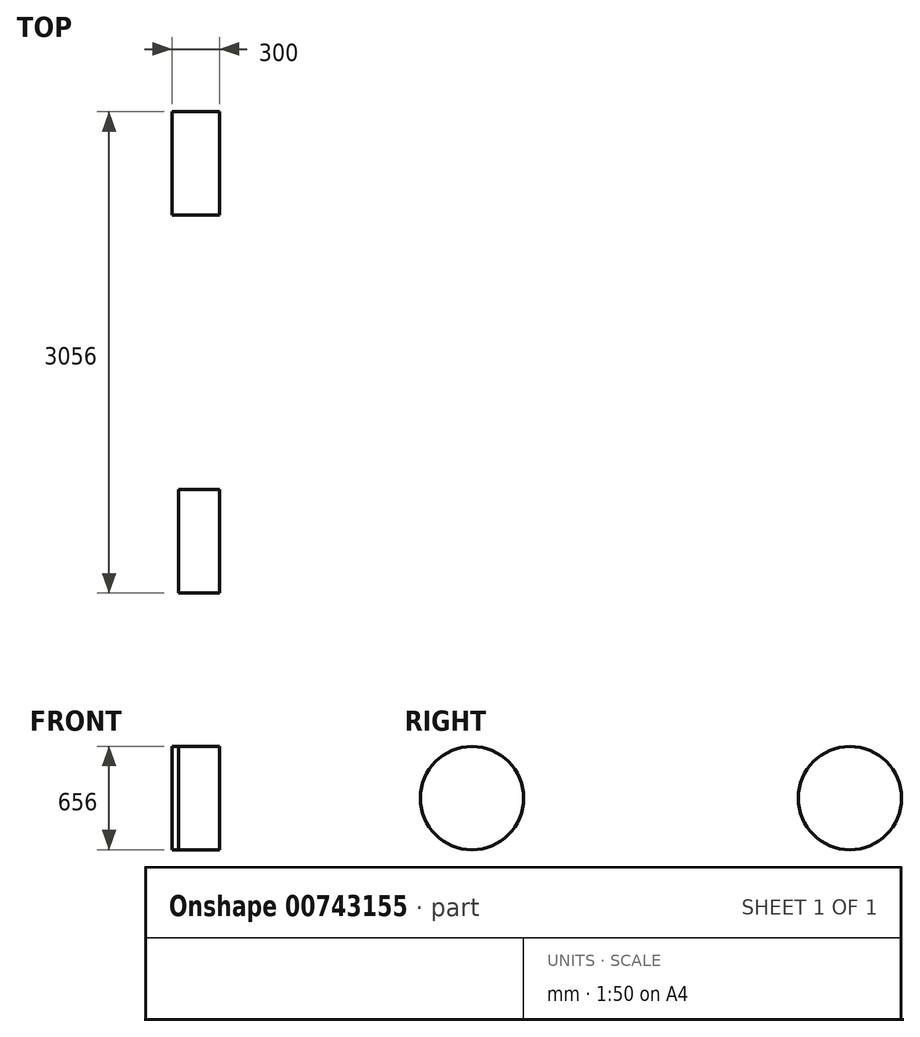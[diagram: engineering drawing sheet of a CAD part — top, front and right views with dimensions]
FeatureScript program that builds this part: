
annotation { "Feature Type Name" : "Feature", "Feature Type Description" : "" }
export const myFeature = defineFeature(function(context is Context, id is Id, definition is map)
    precondition{}
    {
        {
            var Q0;
            Q0=qCreatedBy(makeId("Right.planeOp"),FACE);
            var sketch = newSketch(context, id + "F0", { "sketchPlane" : qUnion([Q0])});
            skCircle(sketch, "E0", {"center": v(-865.86, -88.17) * mm, "radius": 328 * mm});
            skCircle(sketch, "E1", {"center": v(1534.14, -88.17) * mm, "radius": 328 * mm});
            skArc(sketch, "E2", {"start": v(-515.86, -88.17) * mm, "mid": v(-865.86, 261.83) * mm, "end": v(-1215.86, -88.17) * mm});
            skArc(sketch, "E3", {"start": v(1884.14, -88.17) * mm, "mid": v(1534.14, 261.83) * mm, "end": v(1184.14, -88.17) * mm});
            skCircle(sketch, "E4", {"center": v(-865.86, -88.17) * mm, "radius": 254 * mm});
            skCircle(sketch, "E5", {"center": v(1534.14, -88.17) * mm, "radius": 254 * mm});
            skLineSegment(sketch, "E6", {"start": v(-515.86, -88.17) * mm, "end": v(-515.86, -342.17) * mm});
            skLineSegment(sketch, "E7", {"start": v(-515.86, -342.17) * mm, "end": v(1184.14, -342.17) * mm});
            skLineSegment(sketch, "E8", {"start": v(1184.14, -342.17) * mm, "end": v(1184.14, -88.17) * mm});
            skLineSegment(sketch, "E9", {"start": v(-865.86, -342.17) * mm, "end": v(1534.14, -342.17) * mm, "construction": true});
            skLineSegment(sketch, "E10", {"start": v(-1215.86, -88.17) * mm, "end": v(-1215.86, -342.17) * mm});
            skLineSegment(sketch, "E11", {"start": v(-1215.86, -342.17) * mm, "end": v(-1715.86, -342.17) * mm});
            skLineSegment(sketch, "E12", {"start": v(-865.86, -342.17) * mm, "end": v(-2003.44, -342.17) * mm, "construction": true});
            skLineSegment(sketch, "E13", {"start": v(-1715.86, -342.17) * mm, "end": v(-1615.86, -282.17) * mm});
            skLineSegment(sketch, "E14", {"start": v(-1615.86, -282.17) * mm, "end": v(-1715.86, -62.17) * mm});
            skFitSpline(sketch, "E15", {"points": [v(-1715.86, -62.17) * mm, v(-865.86, 311.83) * mm, v(-65.86, 237.83) * mm, v(694.14, 237.83) * mm, v(1534.14, 311.83) * mm, v(1999.14, 201.83) * mm], "startDerivative": vector(5740.96, 4050.88) * mm, "endDerivative": vector(2088.55, 269.29) * mm});
            skFitSpline(sketch, "E16", {"points": [v(1999.14, 201.83) * mm, v(1884.14, -88.17) * mm], "startDerivative": vector(-161.5, -271.03) * mm, "endDerivative": vector(-344.1, -698.66) * mm});
            skLineSegment(sketch, "E17", {"start": v(-605.86, 300.17) * mm, "end": v(-105.86, 631.83) * mm});
            skFitSpline(sketch, "E18", {"points": [v(-105.86, 631.83) * mm, v(705.51, 627.45) * mm, v(1401.65, 430.3) * mm], "startDerivative": vector(1350.4, 204.52) * mm, "endDerivative": vector(1584.08, -729.05) * mm});
            skFitSpline(sketch, "E19", {"points": [v(1401.65, 430.3) * mm, v(1819.73, 233.23) * mm], "startDerivative": vector(436.87, -218.43) * mm, "endDerivative": vector(749.4, -276.18) * mm});
            skLineSegment(sketch, "E20", {"start": v(-125.86, 244.37) * mm, "end": v(194.14, 654.25) * mm});
            skLineSegment(sketch, "E21", {"start": v(224.14, 654.6) * mm, "end": v(-5.86, 231.93) * mm});
            skSolve(sketch);
        }
        {
            var Q0;
            Q0=qCreatedBy(makeId("Right.planeOp"),FACE);
            cPlane(context, id + "F1", {"entities" : qUnion([Q0]), "cplaneType" : CPlaneType.OFFSET, "offset" : 212.5 * mm, "width" : 150 * mm, "height" : 150 * mm});
        }
        {
            var Q0;
            Q0=qCreatedBy(id+"F1.planeOp",FACE);
            var sketch = newSketch(context, id + "F2", { "sketchPlane" : qUnion([Q0])});
            skLineSegment(sketch, "E22", {"start": v(-515.86, -342.17) * mm, "end": v(1184.14, -342.17) * mm});
            skLineSegment(sketch, "E23", {"start": v(-865.86, -342.17) * mm, "end": v(1534.14, -342.17) * mm, "construction": true});
            skLineSegment(sketch, "E24", {"start": v(-1215.86, -342.17) * mm, "end": v(-1715.86, -342.17) * mm});
            skLineSegment(sketch, "E25", {"start": v(-865.86, -342.17) * mm, "end": v(-2003.44, -342.17) * mm, "construction": true});
            skLineSegment(sketch, "E26", {"start": v(-1715.86, -342.17) * mm, "end": v(-1615.86, -282.17) * mm});
            skLineSegment(sketch, "E27", {"start": v(-1615.86, -282.17) * mm, "end": v(-1715.86, -62.17) * mm});
            skFitSpline(sketch, "E28", {"points": [v(-1715.86, -62.17) * mm, v(-865.86, 294.43) * mm, v(-125.86, 244.37) * mm, v(694.14, 237.83) * mm, v(1534.14, 311.83) * mm, v(2029.14, 231.83) * mm], "startDerivative": vector(7164.4, 1851.46) * mm, "endDerivative": vector(1582.19, 801.63) * mm});
            skFitSpline(sketch, "E29", {"points": [v(2029.14, 231.83) * mm, v(1884.14, -88.17) * mm], "startDerivative": vector(-239.57, -231.11) * mm, "endDerivative": vector(-332.35, -626.96) * mm});
            skLineSegment(sketch, "E30", {"start": v(-605.86, 300.17) * mm, "end": v(-94.74, 614.43) * mm});
            skFitSpline(sketch, "E31", {"points": [v(-94.74, 614.43) * mm, v(705.51, 627.45) * mm, v(1401.65, 430.3) * mm], "startDerivative": vector(1350.4, 204.52) * mm, "endDerivative": vector(1584.08, -729.05) * mm});
            skFitSpline(sketch, "E32", {"points": [v(1401.65, 430.3) * mm, v(1873.2, 234.18) * mm], "startDerivative": vector(451.4, -244.97) * mm, "endDerivative": vector(757.42, -207.47) * mm});
            skLineSegment(sketch, "E33", {"start": v(-1215.86, -342.17) * mm, "end": v(-515.86, -342.17) * mm});
            skLineSegment(sketch, "E34", {"start": v(1184.14, -342.17) * mm, "end": v(1884.14, -88.17) * mm});
            skSolve(sketch);
        }
        {
            var Q0;
            Q0=qCreatedBy(id+"F1.planeOp",FACE);
            cPlane(context, id + "F3", {"entities" : qUnion([Q0]), "cplaneType" : CPlaneType.OFFSET, "offset" : 212.5 * mm, "width" : 150 * mm, "height" : 150 * mm});
        }
        {
            var Q0;
            Q0=qCreatedBy(id+"F3.planeOp",FACE);
            var sketch = newSketch(context, id + "F4", { "sketchPlane" : qUnion([Q0])});
            skCircle(sketch, "E35", {"center": v(-865.86, -88.17) * mm, "radius": 328 * mm});
            skCircle(sketch, "E36", {"center": v(1534.14, -88.17) * mm, "radius": 328 * mm});
            skArc(sketch, "E37", {"start": v(-515.86, -88.17) * mm, "mid": v(-865.86, 261.83) * mm, "end": v(-1215.86, -88.17) * mm});
            skArc(sketch, "E38", {"start": v(1884.14, -88.17) * mm, "mid": v(1534.14, 261.83) * mm, "end": v(1184.14, -88.17) * mm});
            skCircle(sketch, "E39", {"center": v(-865.86, -88.17) * mm, "radius": 254 * mm});
            skCircle(sketch, "E40", {"center": v(1534.14, -88.17) * mm, "radius": 254 * mm});
            skLineSegment(sketch, "E41", {"start": v(-515.86, -88.17) * mm, "end": v(-515.86, -342.17) * mm});
            skLineSegment(sketch, "E42", {"start": v(-515.86, -342.17) * mm, "end": v(1184.14, -342.17) * mm});
            skLineSegment(sketch, "E43", {"start": v(1184.14, -342.17) * mm, "end": v(1184.14, -88.17) * mm});
            skLineSegment(sketch, "E44", {"start": v(-865.86, -342.17) * mm, "end": v(1534.14, -342.17) * mm, "construction": true});
            skLineSegment(sketch, "E45", {"start": v(-1215.86, -88.17) * mm, "end": v(-1215.86, -342.17) * mm});
            skLineSegment(sketch, "E46", {"start": v(-1215.86, -342.17) * mm, "end": v(-1715.86, -342.17) * mm});
            skLineSegment(sketch, "E47", {"start": v(-865.86, -342.17) * mm, "end": v(-2003.44, -342.17) * mm, "construction": true});
            skLineSegment(sketch, "E48", {"start": v(-1715.86, -342.17) * mm, "end": v(-1615.86, -282.17) * mm});
            skLineSegment(sketch, "E49", {"start": v(-1615.86, -282.17) * mm, "end": v(-1715.86, -62.17) * mm});
            skFitSpline(sketch, "E50", {"points": [v(-1715.86, -62.17) * mm, v(-865.86, 311.83) * mm, v(-65.86, 237.83) * mm, v(694.14, 237.83) * mm, v(1534.14, 311.83) * mm, v(1999.14, 201.83) * mm], "startDerivative": vector(5740.96, 4050.88) * mm, "endDerivative": vector(2088.55, 269.29) * mm});
            skFitSpline(sketch, "E51", {"points": [v(1999.14, 201.83) * mm, v(1884.14, -88.17) * mm], "startDerivative": vector(-161.5, -271.03) * mm, "endDerivative": vector(-344.1, -698.66) * mm});
            skLineSegment(sketch, "E52", {"start": v(-605.86, 300.17) * mm, "end": v(-105.86, 631.83) * mm});
            skFitSpline(sketch, "E53", {"points": [v(-105.86, 631.83) * mm, v(705.51, 627.45) * mm, v(1401.65, 430.3) * mm], "startDerivative": vector(1350.4, 204.52) * mm, "endDerivative": vector(1584.08, -729.05) * mm});
            skFitSpline(sketch, "E54", {"points": [v(1401.65, 430.3) * mm, v(1819.73, 233.23) * mm], "startDerivative": vector(436.87, -218.43) * mm, "endDerivative": vector(749.4, -276.18) * mm});
            skLineSegment(sketch, "E55", {"start": v(-125.86, 244.37) * mm, "end": v(194.14, 654.25) * mm});
            skLineSegment(sketch, "E56", {"start": v(224.14, 654.6) * mm, "end": v(-5.86, 231.93) * mm});
            skSolve(sketch);
        }
        {
            var Q0;
            Q0=qCreatedBy(id+"F3.planeOp",FACE);
            cPlane(context, id + "F5", {"entities" : qUnion([Q0]), "cplaneType" : CPlaneType.OFFSET, "offset" : 212.5 * mm, "width" : 150 * mm, "height" : 150 * mm});
        }
        {
            var Q0;
            Q0=qCreatedBy(id+"F5.planeOp",FACE);
            var sketch = newSketch(context, id + "F6", { "sketchPlane" : qUnion([Q0])});
            skCircle(sketch, "E57", {"center": v(-865.86, -88.17) * mm, "radius": 328 * mm});
            skCircle(sketch, "E58", {"center": v(1534.14, -88.17) * mm, "radius": 328 * mm});
            skArc(sketch, "E59", {"start": v(-515.86, -88.17) * mm, "mid": v(-865.86, 261.83) * mm, "end": v(-1215.86, -88.17) * mm});
            skArc(sketch, "E60", {"start": v(1884.14, -88.17) * mm, "mid": v(1534.14, 261.83) * mm, "end": v(1184.14, -88.17) * mm});
            skCircle(sketch, "E61", {"center": v(-865.86, -88.17) * mm, "radius": 254 * mm});
            skCircle(sketch, "E62", {"center": v(1534.14, -88.17) * mm, "radius": 254 * mm});
            skLineSegment(sketch, "E63", {"start": v(-515.86, -88.17) * mm, "end": v(-515.86, -342.17) * mm});
            skLineSegment(sketch, "E64", {"start": v(-515.86, -342.17) * mm, "end": v(1184.14, -342.17) * mm});
            skLineSegment(sketch, "E65", {"start": v(1184.14, -342.17) * mm, "end": v(1184.14, -88.17) * mm});
            skLineSegment(sketch, "E66", {"start": v(-865.86, -342.17) * mm, "end": v(1534.14, -342.17) * mm, "construction": true});
            skLineSegment(sketch, "E67", {"start": v(-1215.86, -88.17) * mm, "end": v(-1215.86, -342.17) * mm});
            skLineSegment(sketch, "E68", {"start": v(-1215.86, -342.17) * mm, "end": v(-1715.86, -342.17) * mm});
            skLineSegment(sketch, "E69", {"start": v(-865.86, -342.17) * mm, "end": v(-2003.44, -342.17) * mm, "construction": true});
            skLineSegment(sketch, "E70", {"start": v(-1715.86, -342.17) * mm, "end": v(-1615.86, -282.17) * mm});
            skLineSegment(sketch, "E71", {"start": v(-1615.86, -282.17) * mm, "end": v(-1715.86, -62.17) * mm});
            skFitSpline(sketch, "E72", {"points": [v(-1715.86, -62.17) * mm, v(-865.86, 311.83) * mm, v(-65.86, 237.83) * mm, v(694.14, 237.83) * mm, v(1534.14, 311.83) * mm, v(1999.14, 201.83) * mm], "startDerivative": vector(5740.96, 4050.88) * mm, "endDerivative": vector(2088.55, 269.29) * mm});
            skFitSpline(sketch, "E73", {"points": [v(1999.14, 201.83) * mm, v(1884.14, -88.17) * mm], "startDerivative": vector(-161.5, -271.03) * mm, "endDerivative": vector(-344.1, -698.66) * mm});
            skLineSegment(sketch, "E74", {"start": v(-605.86, 300.17) * mm, "end": v(-105.86, 631.83) * mm});
            skFitSpline(sketch, "E75", {"points": [v(-105.86, 631.83) * mm, v(705.51, 627.45) * mm, v(1401.65, 430.3) * mm], "startDerivative": vector(1350.4, 204.52) * mm, "endDerivative": vector(1584.08, -729.05) * mm});
            skFitSpline(sketch, "E76", {"points": [v(1401.65, 430.3) * mm, v(1819.73, 233.23) * mm], "startDerivative": vector(436.87, -218.43) * mm, "endDerivative": vector(749.4, -276.18) * mm});
            skLineSegment(sketch, "E77", {"start": v(-125.86, 244.37) * mm, "end": v(194.14, 654.25) * mm});
            skLineSegment(sketch, "E78", {"start": v(224.14, 654.6) * mm, "end": v(-5.86, 231.93) * mm});
            skSolve(sketch);
        }
        {
            var Q0;
            Q0=makeQuery(id+"F6.imprint","IMPRINT",FACE,{"disambiguationData":[TD([[makeQuery(id+"F6.imprint","IMPRINT",EDGE,{"derivedFrom":sQuery(id+"F6.wireOp",EDGE,"E61")}),1.0]])]});
            var Q1;
            Q1=makeQuery(id+"F6.imprint","IMPRINT",FACE,{"disambiguationData":[TD([[makeQuery(id+"F6.imprint","IMPRINT",EDGE,{"derivedFrom":sQuery(id+"F6.wireOp",EDGE,"E57")}),1.0]])]});
            extrude(context, id + "F7", {"entities" : qUnion([Q0, Q1]), "oppositeDirection" : true, "depth" : 260 * mm, "offsetDistance" : 25 * mm});
        }
        {
            var Q0;
            Q0=makeQuery(id+"F6.imprint","IMPRINT",FACE,{"disambiguationData":[TD([[makeQuery(id+"F6.imprint","IMPRINT",EDGE,{"derivedFrom":sQuery(id+"F6.wireOp",EDGE,"E62")}),1.0]])]});
            var Q1;
            Q1=makeQuery(id+"F6.imprint","IMPRINT",FACE,{"disambiguationData":[TD([[makeQuery(id+"F6.imprint","IMPRINT",EDGE,{"derivedFrom":sQuery(id+"F6.wireOp",EDGE,"E58")}),1.0]])]});
            extrude(context, id + "F8", {"entities" : qUnion([Q0, Q1]), "oppositeDirection" : true, "depth" : 300 * mm, "offsetDistance" : 25 * mm});
        }
        {
            var Q0;
            Q0=sQuery(id+"F2.wireOp",EDGE,"E28");
            var Q1;
            Q1=sQuery(id+"F4.wireOp",EDGE,"E50");
            loft(context, id + "F9", {"bodyType" : ToolBodyType.SURFACE, "wireProfilesArray" : [{ "wireProfileEntities" : qUnion([Q0]) }, { "wireProfileEntities" : qUnion([Q1]) }]});
        }
        {
            var Q0;
            Q0=sQuery(id+"F2.wireOp",EDGE,"E30");
            var Q1;
            Q1=sQuery(id+"F4.wireOp",EDGE,"E52");
            loft(context, id + "F10", {"bodyType" : ToolBodyType.SURFACE, "operationType" : NewBodyOperationType.ADD, "wireProfilesArray" : [{ "wireProfileEntities" : qUnion([Q0]) }, { "wireProfileEntities" : qUnion([Q1]) }]});
        }
        {
            var Q0;
            Q0=sQuery(id+"F2.wireOp",EDGE,"E31");
            var Q1;
            Q1=sQuery(id+"F4.wireOp",EDGE,"E53");
            loft(context, id + "F11", {"bodyType" : ToolBodyType.SURFACE, "wireProfilesArray" : [{ "wireProfileEntities" : qUnion([Q0]) }, { "wireProfileEntities" : qUnion([Q1]) }]});
        }
        {
            var Q0;
            {var subQ4=sQuery(id+"F2.wireOp",EDGE,"E31");Q0=makeQuery(id+"F2.imprint","IMPRINT",FACE,{"disambiguationData":[TD([[makeQuery(id+"F2.imprint","IMPRINT",EDGE,{"derivedFrom":subQ4}),-1.0]])]});}
            var Q1;
            Q1=sQuery(id+"F2.wireOp",EDGE,"E32");
            var Q2;
            Q2=sQuery(id+"F4.wireOp",EDGE,"E54");
            loft(context, id + "F12", {"bodyType" : ToolBodyType.SURFACE, "sheetProfilesArray" : [{ "sheetProfileEntities" : qUnion([Q0]) }], "wireProfilesArray" : [{ "wireProfileEntities" : qUnion([Q1]) }, { "wireProfileEntities" : qUnion([Q2]) }]});
        }
        {
            var Q0;
            Q0=sQuery(id+"F2.wireOp",EDGE,"E27");
            var Q1;
            Q1=sQuery(id+"F4.wireOp",EDGE,"E49");
            loft(context, id + "F13", {"bodyType" : ToolBodyType.SURFACE, "wireProfilesArray" : [{ "wireProfileEntities" : qUnion([Q0]) }, { "wireProfileEntities" : qUnion([Q1]) }]});
        }
        {
            var Q0;
            Q0=sQuery(id+"F2.wireOp",EDGE,"E26");
            var Q1;
            Q1=sQuery(id+"F4.wireOp",EDGE,"E48");
            loft(context, id + "F14", {"bodyType" : ToolBodyType.SURFACE, "wireProfilesArray" : [{ "wireProfileEntities" : qUnion([Q0]) }, { "wireProfileEntities" : qUnion([Q1]) }]});
        }
        {
            var Q0;
            Q0=makeQuery(id+"F2.imprint","IMPRINT",FACE,{"disambiguationData":[TD([[makeQuery(id+"F2.imprint","IMPRINT",EDGE,{"derivedFrom":sQuery(id+"F2.wireOp",EDGE,"E22")}),1.0]])]});
            var Q1;
            Q1=sQuery(id+"F2.wireOp",EDGE,"E24");
            var Q2;
            Q2=sQuery(id+"F4.wireOp",EDGE,"E46");
            loft(context, id + "F15", {"bodyType" : ToolBodyType.SURFACE, "sheetProfilesArray" : [{ "sheetProfileEntities" : qUnion([Q0]) }], "wireProfilesArray" : [{ "wireProfileEntities" : qUnion([Q1]) }, { "wireProfileEntities" : qUnion([Q2]) }]});
        }
        {
            var Q0;
            Q0=sQuery(id+"F4.wireOp",EDGE,"E42");
            var Q1;
            Q1=sQuery(id+"F2.wireOp",EDGE,"E22");
            loft(context, id + "F16", {"bodyType" : ToolBodyType.SURFACE, "wireProfilesArray" : [{ "wireProfileEntities" : qUnion([Q0]) }, { "wireProfileEntities" : qUnion([Q1]) }]});
        }
        {
            var Q0;
            Q0=sQuery(id+"F4.wireOp",EDGE,"E51");
            var Q1;
            Q1=sQuery(id+"F2.wireOp",EDGE,"E29");
            loft(context, id + "F17", {"bodyType" : ToolBodyType.SURFACE, "wireProfilesArray" : [{ "wireProfileEntities" : qUnion([Q0]) }, { "wireProfileEntities" : qUnion([Q1]) }]});
        }
        {
            var Q0;
            Q0=makeQuery(id+"F4.imprint","IMPRINT",FACE,{"disambiguationData":[TD([[makeQuery(id+"F4.imprint","IMPRINT",EDGE,{"derivedFrom":sQuery(id+"F4.wireOp",EDGE,"E37")}),-1.0]])]});
            var Q1;
            Q1=makeQuery(id+"F6.imprint","IMPRINT",FACE,{"disambiguationData":[TD([[makeQuery(id+"F6.imprint","IMPRINT",EDGE,{"derivedFrom":sQuery(id+"F6.wireOp",EDGE,"E59")}),-1.0]])]});
            var Q2;
            Q2=makeQuery(id+"F4.imprint","IMPRINT",FACE,{"disambiguationData":[TD([[makeQuery(id+"F4.imprint","IMPRINT",EDGE,{"derivedFrom":sQuery(id+"F4.wireOp",EDGE,"E37")}),-1.0]])]});
            var Q3;
            Q3=makeQuery(id+"F6.imprint","IMPRINT",FACE,{"disambiguationData":[TD([[makeQuery(id+"F6.imprint","IMPRINT",EDGE,{"derivedFrom":sQuery(id+"F6.wireOp",EDGE,"E59")}),-1.0]])]});
            loft(context, id + "F18", {"bodyType" : ToolBodyType.SURFACE, "sheetProfilesArray" : [{ "sheetProfileEntities" : qUnion([Q0]) }, { "sheetProfileEntities" : qUnion([Q1]) }], "wireProfilesArray" : [{ "wireProfileEntities" : qUnion([Q2]) }, { "wireProfileEntities" : qUnion([Q3]) }]});
        }
    });
